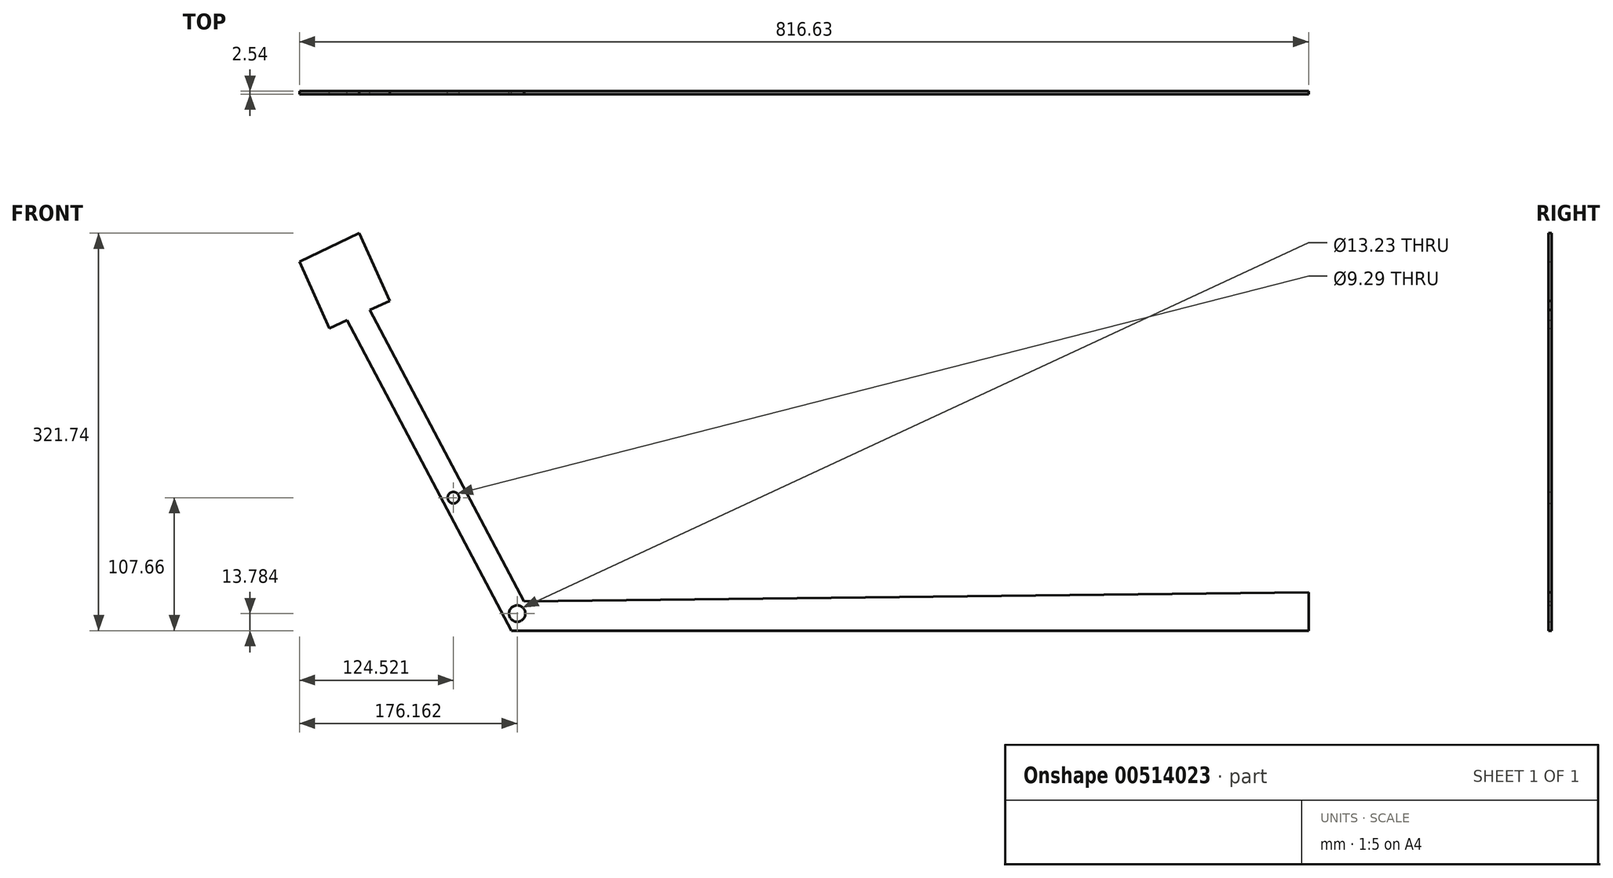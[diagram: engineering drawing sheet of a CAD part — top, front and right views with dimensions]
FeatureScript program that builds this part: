
annotation { "Feature Type Name" : "Feature", "Feature Type Description" : "" }
export const myFeature = defineFeature(function(context is Context, id is Id, definition is map)
    precondition{}
    {
        {
            var Q0;
            Q0=qCreatedBy(makeId("Front.planeOp"),FACE);
            var sketch = newSketch(context, id + "F0", { "sketchPlane" : qUnion([Q0])});
            skLineSegment(sketch, "E0", {"start": v(-413.24, 191) * mm, "end": v(-388.93, 137.17) * mm});
            skLineSegment(sketch, "E1", {"start": v(-388.93, 137.17) * mm, "end": v(-340.09, 159.23) * mm});
            skLineSegment(sketch, "E2", {"start": v(-340.09, 159.23) * mm, "end": v(-364.86, 214.08) * mm});
            skLineSegment(sketch, "E3", {"start": v(-364.86, 214.08) * mm, "end": v(-413.24, 191) * mm});
            skLineSegment(sketch, "E4", {"start": v(-374.75, 143.57) * mm, "end": v(-249.1, -93.88) * mm});
            skLineSegment(sketch, "E5", {"start": v(-231.58, -83.83) * mm, "end": v(-356.32, 151.9) * mm});
            skLineSegment(sketch, "E6", {"start": v(403.39, -107.66) * mm, "end": v(403.39, -76.8) * mm});
            skLineSegment(sketch, "E7", {"start": v(403.39, -76.8) * mm, "end": v(-231.58, -83.83) * mm});
            skLineSegment(sketch, "E8", {"start": v(-249.1, -93.88) * mm, "end": v(-241.81, -107.66) * mm});
            skLineSegment(sketch, "E9", {"start": v(-241.81, -107.66) * mm, "end": v(403.39, -107.66) * mm});
            skCircle(sketch, "E10", {"center": v(-237.08, -93.88) * mm, "radius": 2.14 * mm});
            skCircle(sketch, "E11", {"center": v(-237.08, -93.88) * mm, "radius": 6.62 * mm});
            skCircle(sketch, "E12", {"center": v(-288.72, 0) * mm, "radius": 4.65 * mm});
            skSolve(sketch);
        }
        {
            var Q0;
            {var subQ4=sQuery(id+"F0.wireOp",EDGE,"E0");Q0=makeQuery(id+"F0.imprint","IMPRINT",FACE,{"disambiguationData":[TD([[makeQuery(id+"F0.imprint","IMPRINT",EDGE,{"derivedFrom":subQ4}),1.0]])]});}
            var Q1;
            {var subQ0=sQuery(id+"F0.wireOp",EDGE,"E4");Q1=makeQuery(id+"F0.imprint","IMPRINT",FACE,{"disambiguationData":[TD([[makeQuery(id+"F0.imprint","IMPRINT",EDGE,{"derivedFrom":subQ0}),1.0]])]});}
            extrude(context, id + "F1", {"entities" : qUnion([Q0, Q1]), "depth" : 2.54 * mm, "offsetDistance" : 25.4 * mm});
        }
    });
